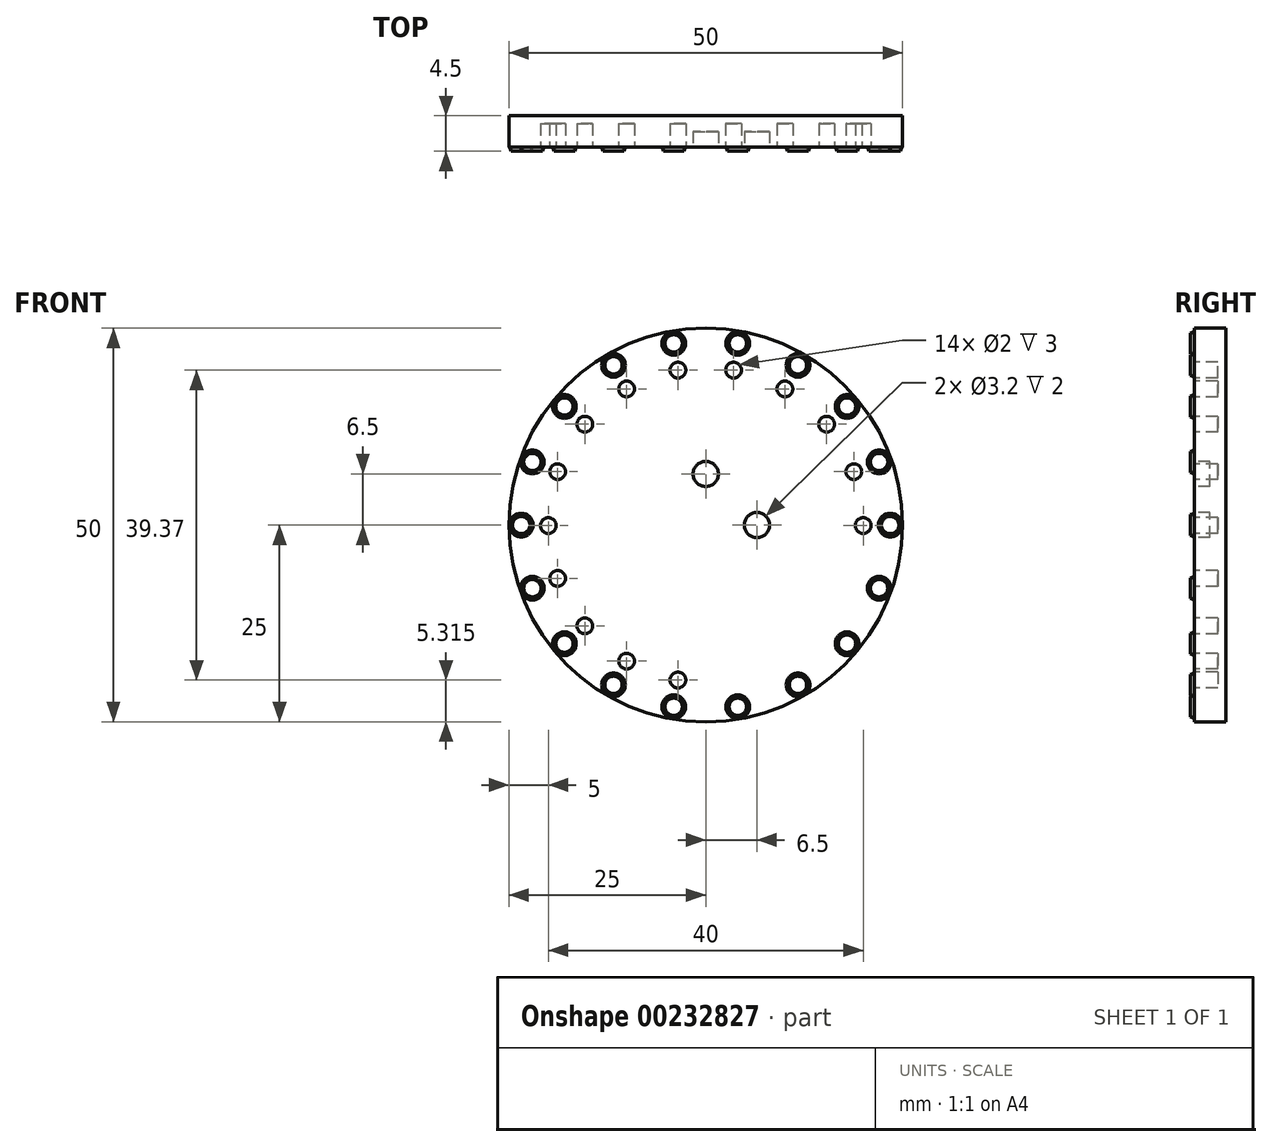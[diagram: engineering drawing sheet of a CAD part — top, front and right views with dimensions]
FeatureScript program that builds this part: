
annotation { "Feature Type Name" : "Feature", "Feature Type Description" : "" }
export const myFeature = defineFeature(function(context is Context, id is Id, definition is map)
    precondition{}
    {
        {
            var Q0;
            Q0=qCreatedBy(makeId("Front.planeOp"),FACE);
            var sketch = newSketch(context, id + "F0", { "sketchPlane" : qUnion([Q0])});
            skCircle(sketch, "E0", {"center": v(0, 0) * mm, "radius": 25 * mm});
            skSolve(sketch);
        }
        {
            var Q0;
            Q0=qSketchRegion(id+"F0",true);
            extrude(context, id + "F1", {"entities" : qUnion([Q0]), "oppositeDirection" : true, "depth" : 4 * mm});
        }
        {
            var Q0;
            Q0=qCreatedBy(makeId("Front.planeOp"),FACE);
            var sketch = newSketch(context, id + "F2", { "sketchPlane" : qUnion([Q0])});
            skCircle(sketch, "E1", {"center": v(0, 0) * mm, "radius": 15 * mm});
            skSolve(sketch);
        }
        {
            var Q0;
            Q0=makeQuery(id+"F0.imprint","IMPRINT",FACE,{"disambiguationData":[TD([[makeQuery(id+"F0.imprint","IMPRINT",EDGE,{"derivedFrom":sQuery(id+"F0.wireOp",EDGE,"E0")}),1.0]])]});
            var sketch = newSketch(context, id + "F3", { "sketchPlane" : qUnion([Q0])});
            skLineSegment(sketch, "E2", {"start": v(-16.87, 0.9) * mm, "end": v(-15.05, 0.07) * mm});
            skLineSegment(sketch, "E3", {"start": v(-15.05, 0.07) * mm, "end": v(-15.05, -0.07) * mm});
            skLineSegment(sketch, "E4", {"start": v(-16.87, 0.9) * mm, "end": v(-16.87, -0.9) * mm});
            skLineSegment(sketch, "E5", {"start": v(-16.87, -0.9) * mm, "end": v(-15.05, -0.07) * mm});
            skCircle(sketch, "E6", {"center": v(0, 6.5) * mm, "radius": 1.6 * mm});
            skCircle(sketch, "E7", {"center": v(6.5, 0) * mm, "radius": 1.6 * mm});
            skSolve(sketch);
        }
        {
            var Q0;
            Q0=makeQuery(id+"F3.imprint","IMPRINT",FACE,{"disambiguationData":[TD([[makeQuery(id+"F3.imprint","IMPRINT",EDGE,{"derivedFrom":sQuery(id+"F3.wireOp",EDGE,"E2")}),1.0]])]});
            var sketch = newSketch(context, id + "F4", { "sketchPlane" : qUnion([Q0])});
            skCircle(sketch, "E8", {"center": v(4.07, 23.08) * mm, "radius": 1.5 * mm});
            skPoint(sketch, "E9.0.midPoint", {"position": v(5.46, 22.51) * mm});
            skCircle(sketch, "E10", {"center": v(4.07, 23.08) * mm, "radius": 1.1 * mm});
            skSolve(sketch);
        }
        {
            var Q0;
            Q0=makeQuery(id+"F4.imprint","IMPRINT",FACE,{"disambiguationData":[TD([[makeQuery(id+"F4.imprint","IMPRINT",EDGE,{"derivedFrom":sQuery(id+"F4.wireOp",EDGE,"E8")}),1.0]])]});
            var Q1;
            Q1=sQuery(id+"F4.wireOp",EDGE,"E10");
            var Q2;
            Q2=sQuery(id+"F4.wireOp",EDGE,"E8");
            extrude(context, id + "F5", {"entities" : qUnion([Q0]), "surfaceEntities" : qUnion([Q1, Q2]), "depth" : 0.5 * mm, "hasDraft" : true, "draftAngle" : 20 * degree, "draftPullDirection" : true});
        }
        {
            var Q0;
            Q0=makeQuery(id+"F5.opExtrude","SWEPT_BODY",BODY,{"disambiguationData":[OSD([sQuery(id+"F4.wireOp",EDGE,"E8"),sQuery(id+"F4.wireOp",EDGE,"E10")])]});
            var Q1;
            Q1=sQuery(id+"F2.wireOp",EDGE,"E1");
            transform(context, id + "F6", {"entities" : qUnion([Q0]), "transformType" : TransformType.ROTATION, "transformAxis" : qUnion([Q1]), "angle" : 20 * degree, "makeCopy" : true});
        }
        {
            var Q0;
            Q0=makeQuery(id+"F6.opPattern","COPY",BODY,{"derivedFrom":makeQuery(id+"F5.opExtrude","SWEPT_BODY",BODY,{"disambiguationData":[OSD([sQuery(id+"F4.wireOp",EDGE,"E8"),sQuery(id+"F4.wireOp",EDGE,"E10")])]}),"instanceName":"1"});
            var Q1;
            Q1=sQuery(id+"F2.wireOp",EDGE,"E1");
            transform(context, id + "F7", {"entities" : qUnion([Q0]), "transformType" : TransformType.ROTATION, "transformAxis" : qUnion([Q1]), "angle" : 20 * degree, "makeCopy" : true});
        }
        {
            var Q0;
            Q0=makeQuery(id+"F7.opPattern","COPY",BODY,{"derivedFrom":makeQuery(id+"F6.opPattern","COPY",BODY,{"derivedFrom":makeQuery(id+"F5.opExtrude","SWEPT_BODY",BODY,{"disambiguationData":[OSD([sQuery(id+"F4.wireOp",EDGE,"E8"),sQuery(id+"F4.wireOp",EDGE,"E10")])]}),"instanceName":"1"}),"instanceName":"1"});
            var Q1;
            Q1=sQuery(id+"F2.wireOp",EDGE,"E1");
            transform(context, id + "F8", {"entities" : qUnion([Q0]), "transformType" : TransformType.ROTATION, "transformAxis" : qUnion([Q1]), "angle" : 20 * degree, "makeCopy" : true});
        }
        {
            var Q0;
            Q0=makeQuery(id+"F8.opPattern","COPY",BODY,{"derivedFrom":makeQuery(id+"F7.opPattern","COPY",BODY,{"derivedFrom":makeQuery(id+"F6.opPattern","COPY",BODY,{"derivedFrom":makeQuery(id+"F5.opExtrude","SWEPT_BODY",BODY,{"disambiguationData":[OSD([sQuery(id+"F4.wireOp",EDGE,"E8"),sQuery(id+"F4.wireOp",EDGE,"E10")])]}),"instanceName":"1"}),"instanceName":"1"}),"instanceName":"1"});
            var Q1;
            Q1=sQuery(id+"F2.wireOp",EDGE,"E1");
            transform(context, id + "F9", {"entities" : qUnion([Q0]), "transformType" : TransformType.ROTATION, "transformAxis" : qUnion([Q1]), "angle" : 20 * degree, "makeCopy" : true});
        }
        {
            var Q0;
            Q0=makeQuery(id+"F9.opPattern","COPY",BODY,{"derivedFrom":makeQuery(id+"F8.opPattern","COPY",BODY,{"derivedFrom":makeQuery(id+"F7.opPattern","COPY",BODY,{"derivedFrom":makeQuery(id+"F6.opPattern","COPY",BODY,{"derivedFrom":makeQuery(id+"F5.opExtrude","SWEPT_BODY",BODY,{"disambiguationData":[OSD([sQuery(id+"F4.wireOp",EDGE,"E8"),sQuery(id+"F4.wireOp",EDGE,"E10")])]}),"instanceName":"1"}),"instanceName":"1"}),"instanceName":"1"}),"instanceName":"1"});
            var Q1;
            Q1=sQuery(id+"F2.wireOp",EDGE,"E1");
            transform(context, id + "F10", {"entities" : qUnion([Q0]), "transformType" : TransformType.ROTATION, "transformAxis" : qUnion([Q1]), "angle" : 20 * degree, "makeCopy" : true});
        }
        {
            var Q0;
            Q0=makeQuery(id+"F5.opExtrude","SWEPT_BODY",BODY,{"disambiguationData":[OSD([sQuery(id+"F4.wireOp",EDGE,"E8"),sQuery(id+"F4.wireOp",EDGE,"E10")])]});
            var Q1;
            Q1=makeQuery(id+"F6.opPattern","COPY",BODY,{"derivedFrom":makeQuery(id+"F5.opExtrude","SWEPT_BODY",BODY,{"disambiguationData":[OSD([sQuery(id+"F4.wireOp",EDGE,"E8"),sQuery(id+"F4.wireOp",EDGE,"E10")])]}),"instanceName":"1"});
            var Q2;
            Q2=makeQuery(id+"F7.opPattern","COPY",BODY,{"derivedFrom":makeQuery(id+"F6.opPattern","COPY",BODY,{"derivedFrom":makeQuery(id+"F5.opExtrude","SWEPT_BODY",BODY,{"disambiguationData":[OSD([sQuery(id+"F4.wireOp",EDGE,"E8"),sQuery(id+"F4.wireOp",EDGE,"E10")])]}),"instanceName":"1"}),"instanceName":"1"});
            var Q3;
            Q3=makeQuery(id+"F8.opPattern","COPY",BODY,{"derivedFrom":makeQuery(id+"F7.opPattern","COPY",BODY,{"derivedFrom":makeQuery(id+"F6.opPattern","COPY",BODY,{"derivedFrom":makeQuery(id+"F5.opExtrude","SWEPT_BODY",BODY,{"disambiguationData":[OSD([sQuery(id+"F4.wireOp",EDGE,"E8"),sQuery(id+"F4.wireOp",EDGE,"E10")])]}),"instanceName":"1"}),"instanceName":"1"}),"instanceName":"1"});
            var Q4;
            Q4=makeQuery(id+"F9.opPattern","COPY",BODY,{"derivedFrom":makeQuery(id+"F8.opPattern","COPY",BODY,{"derivedFrom":makeQuery(id+"F7.opPattern","COPY",BODY,{"derivedFrom":makeQuery(id+"F6.opPattern","COPY",BODY,{"derivedFrom":makeQuery(id+"F5.opExtrude","SWEPT_BODY",BODY,{"disambiguationData":[OSD([sQuery(id+"F4.wireOp",EDGE,"E8"),sQuery(id+"F4.wireOp",EDGE,"E10")])]}),"instanceName":"1"}),"instanceName":"1"}),"instanceName":"1"}),"instanceName":"1"});
            var Q5;
            Q5=makeQuery(id+"F10.opPattern","COPY",BODY,{"derivedFrom":makeQuery(id+"F9.opPattern","COPY",BODY,{"derivedFrom":makeQuery(id+"F8.opPattern","COPY",BODY,{"derivedFrom":makeQuery(id+"F7.opPattern","COPY",BODY,{"derivedFrom":makeQuery(id+"F6.opPattern","COPY",BODY,{"derivedFrom":makeQuery(id+"F5.opExtrude","SWEPT_BODY",BODY,{"disambiguationData":[OSD([sQuery(id+"F4.wireOp",EDGE,"E8"),sQuery(id+"F4.wireOp",EDGE,"E10")])]}),"instanceName":"1"}),"instanceName":"1"}),"instanceName":"1"}),"instanceName":"1"}),"instanceName":"1"});
            var Q6;
            Q6=qCreatedBy(makeId("Top.planeOp"),FACE);
            mirror(context, id + "F11", {"entities" : qUnion([Q0, Q1, Q2, Q3, Q4, Q5]), "mirrorPlane" : qUnion([Q6])});
        }
        {
            var Q0;
            Q0=makeQuery(id+"F11.opPattern","COPY",BODY,{"derivedFrom":makeQuery(id+"F7.opPattern","COPY",BODY,{"derivedFrom":makeQuery(id+"F6.opPattern","COPY",BODY,{"derivedFrom":makeQuery(id+"F5.opExtrude","SWEPT_BODY",BODY,{"disambiguationData":[OSD([sQuery(id+"F4.wireOp",EDGE,"E8"),sQuery(id+"F4.wireOp",EDGE,"E10")])]}),"instanceName":"1"}),"instanceName":"1"}),"instanceName":"1"});
            var Q1;
            Q1=makeQuery(id+"F11.opPattern","COPY",BODY,{"derivedFrom":makeQuery(id+"F8.opPattern","COPY",BODY,{"derivedFrom":makeQuery(id+"F7.opPattern","COPY",BODY,{"derivedFrom":makeQuery(id+"F6.opPattern","COPY",BODY,{"derivedFrom":makeQuery(id+"F5.opExtrude","SWEPT_BODY",BODY,{"disambiguationData":[OSD([sQuery(id+"F4.wireOp",EDGE,"E8"),sQuery(id+"F4.wireOp",EDGE,"E10")])]}),"instanceName":"1"}),"instanceName":"1"}),"instanceName":"1"}),"instanceName":"1"});
            var Q2;
            Q2=makeQuery(id+"F11.opPattern","COPY",BODY,{"derivedFrom":makeQuery(id+"F9.opPattern","COPY",BODY,{"derivedFrom":makeQuery(id+"F8.opPattern","COPY",BODY,{"derivedFrom":makeQuery(id+"F7.opPattern","COPY",BODY,{"derivedFrom":makeQuery(id+"F6.opPattern","COPY",BODY,{"derivedFrom":makeQuery(id+"F5.opExtrude","SWEPT_BODY",BODY,{"disambiguationData":[OSD([sQuery(id+"F4.wireOp",EDGE,"E8"),sQuery(id+"F4.wireOp",EDGE,"E10")])]}),"instanceName":"1"}),"instanceName":"1"}),"instanceName":"1"}),"instanceName":"1"}),"instanceName":"1"});
            var Q3;
            Q3=makeQuery(id+"F10.opPattern","COPY",BODY,{"derivedFrom":makeQuery(id+"F9.opPattern","COPY",BODY,{"derivedFrom":makeQuery(id+"F8.opPattern","COPY",BODY,{"derivedFrom":makeQuery(id+"F7.opPattern","COPY",BODY,{"derivedFrom":makeQuery(id+"F6.opPattern","COPY",BODY,{"derivedFrom":makeQuery(id+"F5.opExtrude","SWEPT_BODY",BODY,{"disambiguationData":[OSD([sQuery(id+"F4.wireOp",EDGE,"E8"),sQuery(id+"F4.wireOp",EDGE,"E10")])]}),"instanceName":"1"}),"instanceName":"1"}),"instanceName":"1"}),"instanceName":"1"}),"instanceName":"1"});
            var Q4;
            Q4=makeQuery(id+"F9.opPattern","COPY",BODY,{"derivedFrom":makeQuery(id+"F8.opPattern","COPY",BODY,{"derivedFrom":makeQuery(id+"F7.opPattern","COPY",BODY,{"derivedFrom":makeQuery(id+"F6.opPattern","COPY",BODY,{"derivedFrom":makeQuery(id+"F5.opExtrude","SWEPT_BODY",BODY,{"disambiguationData":[OSD([sQuery(id+"F4.wireOp",EDGE,"E8"),sQuery(id+"F4.wireOp",EDGE,"E10")])]}),"instanceName":"1"}),"instanceName":"1"}),"instanceName":"1"}),"instanceName":"1"});
            var Q5;
            Q5=makeQuery(id+"F8.opPattern","COPY",BODY,{"derivedFrom":makeQuery(id+"F7.opPattern","COPY",BODY,{"derivedFrom":makeQuery(id+"F6.opPattern","COPY",BODY,{"derivedFrom":makeQuery(id+"F5.opExtrude","SWEPT_BODY",BODY,{"disambiguationData":[OSD([sQuery(id+"F4.wireOp",EDGE,"E8"),sQuery(id+"F4.wireOp",EDGE,"E10")])]}),"instanceName":"1"}),"instanceName":"1"}),"instanceName":"1"});
            var Q6;
            Q6=makeQuery(id+"F7.opPattern","COPY",BODY,{"derivedFrom":makeQuery(id+"F6.opPattern","COPY",BODY,{"derivedFrom":makeQuery(id+"F5.opExtrude","SWEPT_BODY",BODY,{"disambiguationData":[OSD([sQuery(id+"F4.wireOp",EDGE,"E8"),sQuery(id+"F4.wireOp",EDGE,"E10")])]}),"instanceName":"1"}),"instanceName":"1"});
            var Q7;
            Q7=qCreatedBy(makeId("Right.planeOp"),FACE);
            mirror(context, id + "F12", {"operationType" : NewBodyOperationType.ADD, "entities" : qUnion([Q0, Q1, Q2, Q3, Q4, Q5, Q6]), "mirrorPlane" : qUnion([Q7])});
        }
        {
            var Q0;
            Q0=makeQuery(id+"F3.imprint","IMPRINT",FACE,{"disambiguationData":[TD([[makeQuery(id+"F3.imprint","IMPRINT",EDGE,{"derivedFrom":sQuery(id+"F3.wireOp",EDGE,"E2")}),1.0]])]});
            var sketch = newSketch(context, id + "F13", { "sketchPlane" : qUnion([Q0])});
            skCircle(sketch, "E11", {"center": v(-3.53, 19.69) * mm, "radius": 1 * mm});
            skSolve(sketch);
        }
        {
            var Q0;
            Q0=makeQuery(id+"F13.imprint","IMPRINT",FACE,{"disambiguationData":[TD([[makeQuery(id+"F13.imprint","IMPRINT",EDGE,{"derivedFrom":sQuery(id+"F13.wireOp",EDGE,"E11")}),1.0]])]});
            var Q1;
            Q1=sQuery(id+"F13.wireOp",EDGE,"E11");
            extrude(context, id + "F14", {"entities" : qUnion([Q0]), "surfaceEntities" : qUnion([Q1]), "oppositeDirection" : true, "depth" : 3 * mm});
        }
        {
            var Q0;
            Q0=makeQuery(id+"F14.opExtrude","SWEPT_BODY",BODY,{"disambiguationData":[OSD([sQuery(id+"F13.wireOp",EDGE,"E11")])]});
            var Q1;
            Q1=sQuery(id+"F2.wireOp",EDGE,"E1");
            transform(context, id + "F15", {"entities" : qUnion([Q0]), "transformType" : TransformType.ROTATION, "transformAxis" : qUnion([Q1]), "angle" : 20 * degree, "makeCopy" : true});
        }
        {
            var Q0;
            Q0=makeQuery(id+"F15.opPattern","COPY",BODY,{"derivedFrom":makeQuery(id+"F14.opExtrude","SWEPT_BODY",BODY,{"disambiguationData":[OSD([sQuery(id+"F13.wireOp",EDGE,"E11")])]}),"instanceName":"1"});
            var Q1;
            Q1=sQuery(id+"F2.wireOp",EDGE,"E1");
            transform(context, id + "F16", {"entities" : qUnion([Q0]), "transformType" : TransformType.ROTATION, "transformAxis" : qUnion([Q1]), "angle" : 20 * degree, "makeCopy" : true});
        }
        {
            var Q0;
            Q0=makeQuery(id+"F16.opPattern","COPY",BODY,{"derivedFrom":makeQuery(id+"F15.opPattern","COPY",BODY,{"derivedFrom":makeQuery(id+"F14.opExtrude","SWEPT_BODY",BODY,{"disambiguationData":[OSD([sQuery(id+"F13.wireOp",EDGE,"E11")])]}),"instanceName":"1"}),"instanceName":"1"});
            var Q1;
            Q1=sQuery(id+"F2.wireOp",EDGE,"E1");
            transform(context, id + "F17", {"entities" : qUnion([Q0]), "transformType" : TransformType.ROTATION, "transformAxis" : qUnion([Q1]), "angle" : 20 * degree, "makeCopy" : true});
        }
        {
            var Q0;
            Q0=makeQuery(id+"F17.opPattern","COPY",BODY,{"derivedFrom":makeQuery(id+"F16.opPattern","COPY",BODY,{"derivedFrom":makeQuery(id+"F15.opPattern","COPY",BODY,{"derivedFrom":makeQuery(id+"F14.opExtrude","SWEPT_BODY",BODY,{"disambiguationData":[OSD([sQuery(id+"F13.wireOp",EDGE,"E11")])]}),"instanceName":"1"}),"instanceName":"1"}),"instanceName":"1"});
            var Q1;
            Q1=sQuery(id+"F2.wireOp",EDGE,"E1");
            transform(context, id + "F18", {"entities" : qUnion([Q0]), "transformType" : TransformType.ROTATION, "transformAxis" : qUnion([Q1]), "angle" : 20 * degree, "makeCopy" : true});
        }
        {
            var Q0;
            Q0=makeQuery(id+"F14.opExtrude","SWEPT_BODY",BODY,{"disambiguationData":[OSD([sQuery(id+"F13.wireOp",EDGE,"E11")])]});
            var Q1;
            Q1=makeQuery(id+"F16.opPattern","COPY",BODY,{"derivedFrom":makeQuery(id+"F15.opPattern","COPY",BODY,{"derivedFrom":makeQuery(id+"F14.opExtrude","SWEPT_BODY",BODY,{"disambiguationData":[OSD([sQuery(id+"F13.wireOp",EDGE,"E11")])]}),"instanceName":"1"}),"instanceName":"1"});
            var Q2;
            Q2=makeQuery(id+"F17.opPattern","COPY",BODY,{"derivedFrom":makeQuery(id+"F16.opPattern","COPY",BODY,{"derivedFrom":makeQuery(id+"F15.opPattern","COPY",BODY,{"derivedFrom":makeQuery(id+"F14.opExtrude","SWEPT_BODY",BODY,{"disambiguationData":[OSD([sQuery(id+"F13.wireOp",EDGE,"E11")])]}),"instanceName":"1"}),"instanceName":"1"}),"instanceName":"1"});
            var Q3;
            Q3=makeQuery(id+"F15.opPattern","COPY",BODY,{"derivedFrom":makeQuery(id+"F14.opExtrude","SWEPT_BODY",BODY,{"disambiguationData":[OSD([sQuery(id+"F13.wireOp",EDGE,"E11")])]}),"instanceName":"1"});
            var Q4;
            Q4=makeQuery(id+"F18.opPattern","COPY",BODY,{"derivedFrom":makeQuery(id+"F17.opPattern","COPY",BODY,{"derivedFrom":makeQuery(id+"F16.opPattern","COPY",BODY,{"derivedFrom":makeQuery(id+"F15.opPattern","COPY",BODY,{"derivedFrom":makeQuery(id+"F14.opExtrude","SWEPT_BODY",BODY,{"disambiguationData":[OSD([sQuery(id+"F13.wireOp",EDGE,"E11")])]}),"instanceName":"1"}),"instanceName":"1"}),"instanceName":"1"}),"instanceName":"1"});
            var Q5;
            Q5=qCreatedBy(makeId("Right.planeOp"),FACE);
            mirror(context, id + "F19", {"entities" : qUnion([Q0, Q1, Q2, Q3, Q4]), "mirrorPlane" : qUnion([Q5])});
        }
        {
            var Q0;
            Q0=makeQuery(id+"F17.opPattern","COPY",BODY,{"derivedFrom":makeQuery(id+"F16.opPattern","COPY",BODY,{"derivedFrom":makeQuery(id+"F15.opPattern","COPY",BODY,{"derivedFrom":makeQuery(id+"F14.opExtrude","SWEPT_BODY",BODY,{"disambiguationData":[OSD([sQuery(id+"F13.wireOp",EDGE,"E11")])]}),"instanceName":"1"}),"instanceName":"1"}),"instanceName":"1"});
            var Q1;
            Q1=makeQuery(id+"F16.opPattern","COPY",BODY,{"derivedFrom":makeQuery(id+"F15.opPattern","COPY",BODY,{"derivedFrom":makeQuery(id+"F14.opExtrude","SWEPT_BODY",BODY,{"disambiguationData":[OSD([sQuery(id+"F13.wireOp",EDGE,"E11")])]}),"instanceName":"1"}),"instanceName":"1"});
            var Q2;
            Q2=makeQuery(id+"F15.opPattern","COPY",BODY,{"derivedFrom":makeQuery(id+"F14.opExtrude","SWEPT_BODY",BODY,{"disambiguationData":[OSD([sQuery(id+"F13.wireOp",EDGE,"E11")])]}),"instanceName":"1"});
            var Q3;
            Q3=makeQuery(id+"F14.opExtrude","SWEPT_BODY",BODY,{"disambiguationData":[OSD([sQuery(id+"F13.wireOp",EDGE,"E11")])]});
            var Q4;
            Q4=qCreatedBy(makeId("Top.planeOp"),FACE);
            mirror(context, id + "F20", {"entities" : qUnion([Q0, Q1, Q2, Q3]), "mirrorPlane" : qUnion([Q4])});
        }
        {
            var Q0;
            Q0=makeQuery(id+"F14.opExtrude","SWEPT_BODY",BODY,{"disambiguationData":[OSD([sQuery(id+"F13.wireOp",EDGE,"E11")])]});
            var Q1;
            Q1=makeQuery(id+"F15.opPattern","COPY",BODY,{"derivedFrom":makeQuery(id+"F14.opExtrude","SWEPT_BODY",BODY,{"disambiguationData":[OSD([sQuery(id+"F13.wireOp",EDGE,"E11")])]}),"instanceName":"1"});
            var Q2;
            Q2=makeQuery(id+"F16.opPattern","COPY",BODY,{"derivedFrom":makeQuery(id+"F15.opPattern","COPY",BODY,{"derivedFrom":makeQuery(id+"F14.opExtrude","SWEPT_BODY",BODY,{"disambiguationData":[OSD([sQuery(id+"F13.wireOp",EDGE,"E11")])]}),"instanceName":"1"}),"instanceName":"1"});
            var Q3;
            Q3=makeQuery(id+"F17.opPattern","COPY",BODY,{"derivedFrom":makeQuery(id+"F16.opPattern","COPY",BODY,{"derivedFrom":makeQuery(id+"F15.opPattern","COPY",BODY,{"derivedFrom":makeQuery(id+"F14.opExtrude","SWEPT_BODY",BODY,{"disambiguationData":[OSD([sQuery(id+"F13.wireOp",EDGE,"E11")])]}),"instanceName":"1"}),"instanceName":"1"}),"instanceName":"1"});
            var Q4;
            Q4=makeQuery(id+"F18.opPattern","COPY",BODY,{"derivedFrom":makeQuery(id+"F17.opPattern","COPY",BODY,{"derivedFrom":makeQuery(id+"F16.opPattern","COPY",BODY,{"derivedFrom":makeQuery(id+"F15.opPattern","COPY",BODY,{"derivedFrom":makeQuery(id+"F14.opExtrude","SWEPT_BODY",BODY,{"disambiguationData":[OSD([sQuery(id+"F13.wireOp",EDGE,"E11")])]}),"instanceName":"1"}),"instanceName":"1"}),"instanceName":"1"}),"instanceName":"1"});
            var Q5;
            Q5=makeQuery(id+"F1HHIMMmEWS94l6_5.1.F19.opPattern","COPY",BODY,{"derivedFrom":makeQuery(id+"F18.opPattern","COPY",BODY,{"derivedFrom":makeQuery(id+"F17.opPattern","COPY",BODY,{"derivedFrom":makeQuery(id+"F16.opPattern","COPY",BODY,{"derivedFrom":makeQuery(id+"F15.opPattern","COPY",BODY,{"derivedFrom":makeQuery(id+"F14.opExtrude","SWEPT_BODY",BODY,{"disambiguationData":[OSD([sQuery(id+"F13.wireOp",EDGE,"E11")])]}),"instanceName":"1"}),"instanceName":"1"}),"instanceName":"1"}),"instanceName":"1"}),"instanceName":"1"});
            var Q6;
            Q6=makeQuery(id+"F19.opPattern","COPY",BODY,{"derivedFrom":makeQuery(id+"F14.opExtrude","SWEPT_BODY",BODY,{"disambiguationData":[OSD([sQuery(id+"F13.wireOp",EDGE,"E11")])]}),"instanceName":"1"});
            var Q7;
            Q7=makeQuery(id+"F19.opPattern","COPY",BODY,{"derivedFrom":makeQuery(id+"F15.opPattern","COPY",BODY,{"derivedFrom":makeQuery(id+"F14.opExtrude","SWEPT_BODY",BODY,{"disambiguationData":[OSD([sQuery(id+"F13.wireOp",EDGE,"E11")])]}),"instanceName":"1"}),"instanceName":"1"});
            var Q8;
            Q8=makeQuery(id+"F19.opPattern","COPY",BODY,{"derivedFrom":makeQuery(id+"F16.opPattern","COPY",BODY,{"derivedFrom":makeQuery(id+"F15.opPattern","COPY",BODY,{"derivedFrom":makeQuery(id+"F14.opExtrude","SWEPT_BODY",BODY,{"disambiguationData":[OSD([sQuery(id+"F13.wireOp",EDGE,"E11")])]}),"instanceName":"1"}),"instanceName":"1"}),"instanceName":"1"});
            var Q9;
            Q9=makeQuery(id+"F19.opPattern","COPY",BODY,{"derivedFrom":makeQuery(id+"F18.opPattern","COPY",BODY,{"derivedFrom":makeQuery(id+"F17.opPattern","COPY",BODY,{"derivedFrom":makeQuery(id+"F16.opPattern","COPY",BODY,{"derivedFrom":makeQuery(id+"F15.opPattern","COPY",BODY,{"derivedFrom":makeQuery(id+"F14.opExtrude","SWEPT_BODY",BODY,{"disambiguationData":[OSD([sQuery(id+"F13.wireOp",EDGE,"E11")])]}),"instanceName":"1"}),"instanceName":"1"}),"instanceName":"1"}),"instanceName":"1"}),"instanceName":"1"});
            var Q10;
            Q10=makeQuery(id+"F20.opPattern","COPY",BODY,{"derivedFrom":makeQuery(id+"F14.opExtrude","SWEPT_BODY",BODY,{"disambiguationData":[OSD([sQuery(id+"F13.wireOp",EDGE,"E11")])]}),"instanceName":"1"});
            var Q11;
            Q11=makeQuery(id+"F19.opPattern","COPY",BODY,{"derivedFrom":makeQuery(id+"F17.opPattern","COPY",BODY,{"derivedFrom":makeQuery(id+"F16.opPattern","COPY",BODY,{"derivedFrom":makeQuery(id+"F15.opPattern","COPY",BODY,{"derivedFrom":makeQuery(id+"F14.opExtrude","SWEPT_BODY",BODY,{"disambiguationData":[OSD([sQuery(id+"F13.wireOp",EDGE,"E11")])]}),"instanceName":"1"}),"instanceName":"1"}),"instanceName":"1"}),"instanceName":"1"});
            var Q12;
            Q12=makeQuery(id+"F20.opPattern","COPY",BODY,{"derivedFrom":makeQuery(id+"F15.opPattern","COPY",BODY,{"derivedFrom":makeQuery(id+"F14.opExtrude","SWEPT_BODY",BODY,{"disambiguationData":[OSD([sQuery(id+"F13.wireOp",EDGE,"E11")])]}),"instanceName":"1"}),"instanceName":"1"});
            var Q13;
            Q13=makeQuery(id+"F20.opPattern","COPY",BODY,{"derivedFrom":makeQuery(id+"F16.opPattern","COPY",BODY,{"derivedFrom":makeQuery(id+"F15.opPattern","COPY",BODY,{"derivedFrom":makeQuery(id+"F14.opExtrude","SWEPT_BODY",BODY,{"disambiguationData":[OSD([sQuery(id+"F13.wireOp",EDGE,"E11")])]}),"instanceName":"1"}),"instanceName":"1"}),"instanceName":"1"});
            var Q14;
            Q14=makeQuery(id+"F20.opPattern","COPY",BODY,{"derivedFrom":makeQuery(id+"F17.opPattern","COPY",BODY,{"derivedFrom":makeQuery(id+"F16.opPattern","COPY",BODY,{"derivedFrom":makeQuery(id+"F15.opPattern","COPY",BODY,{"derivedFrom":makeQuery(id+"F14.opExtrude","SWEPT_BODY",BODY,{"disambiguationData":[OSD([sQuery(id+"F13.wireOp",EDGE,"E11")])]}),"instanceName":"1"}),"instanceName":"1"}),"instanceName":"1"}),"instanceName":"1"});
            var Q15;
            Q15=makeQuery(id+"F1HHIMMmEWS94l6_5.1.F19.opPattern","COPY",BODY,{"derivedFrom":makeQuery(id+"F14.opExtrude","SWEPT_BODY",BODY,{"disambiguationData":[OSD([sQuery(id+"F13.wireOp",EDGE,"E11")])]}),"instanceName":"1"});
            var Q16;
            Q16=makeQuery(id+"F1HHIMMmEWS94l6_5.1.F19.opPattern","COPY",BODY,{"derivedFrom":makeQuery(id+"F16.opPattern","COPY",BODY,{"derivedFrom":makeQuery(id+"F15.opPattern","COPY",BODY,{"derivedFrom":makeQuery(id+"F14.opExtrude","SWEPT_BODY",BODY,{"disambiguationData":[OSD([sQuery(id+"F13.wireOp",EDGE,"E11")])]}),"instanceName":"1"}),"instanceName":"1"}),"instanceName":"1"});
            var Q17;
            Q17=makeQuery(id+"F1HHIMMmEWS94l6_5.1.F19.opPattern","COPY",BODY,{"derivedFrom":makeQuery(id+"F17.opPattern","COPY",BODY,{"derivedFrom":makeQuery(id+"F16.opPattern","COPY",BODY,{"derivedFrom":makeQuery(id+"F15.opPattern","COPY",BODY,{"derivedFrom":makeQuery(id+"F14.opExtrude","SWEPT_BODY",BODY,{"disambiguationData":[OSD([sQuery(id+"F13.wireOp",EDGE,"E11")])]}),"instanceName":"1"}),"instanceName":"1"}),"instanceName":"1"}),"instanceName":"1"});
            var Q18;
            Q18=makeQuery(id+"F1HHIMMmEWS94l6_5.1.F19.opPattern","COPY",BODY,{"derivedFrom":makeQuery(id+"F15.opPattern","COPY",BODY,{"derivedFrom":makeQuery(id+"F14.opExtrude","SWEPT_BODY",BODY,{"disambiguationData":[OSD([sQuery(id+"F13.wireOp",EDGE,"E11")])]}),"instanceName":"1"}),"instanceName":"1"});
            var Q19;
            Q19=makeQuery(id+"F1.opExtrude","SWEPT_BODY",BODY,{"disambiguationData":[OSD([sQuery(id+"F0.wireOp",EDGE,"E0")])]});
            booleanBodies(context, id + "F21", {"operationType" : BooleanOperationType.SUBTRACTION, "tools" : qUnion([Q0, Q1, Q2, Q3, Q4, Q5, Q6, Q7, Q8, Q9, Q10, Q11, Q12, Q13, Q14, Q15, Q16, Q17, Q18]), "targets" : qUnion([Q19])});
        }
        {
            var Q0;
            Q0=makeQuery(id+"F3.imprint","IMPRINT",FACE,{"disambiguationData":[TD([[makeQuery(id+"F3.imprint","IMPRINT",EDGE,{"derivedFrom":sQuery(id+"F3.wireOp",EDGE,"E7")}),1.0]])]});
            var Q1;
            Q1=makeQuery(id+"F3.imprint","IMPRINT",FACE,{"disambiguationData":[TD([[makeQuery(id+"F3.imprint","IMPRINT",EDGE,{"derivedFrom":sQuery(id+"F3.wireOp",EDGE,"E6")}),1.0]])]});
            var Q2;
            Q2=sQuery(id+"F3.wireOp",EDGE,"E6");
            var Q3;
            Q3=sQuery(id+"F3.wireOp",EDGE,"E7");
            extrude(context, id + "F22", {"entities" : qUnion([Q0, Q1]), "operationType" : NewBodyOperationType.REMOVE, "surfaceEntities" : qUnion([Q2, Q3]), "oppositeDirection" : true, "depth" : 2 * mm});
        }
    });
